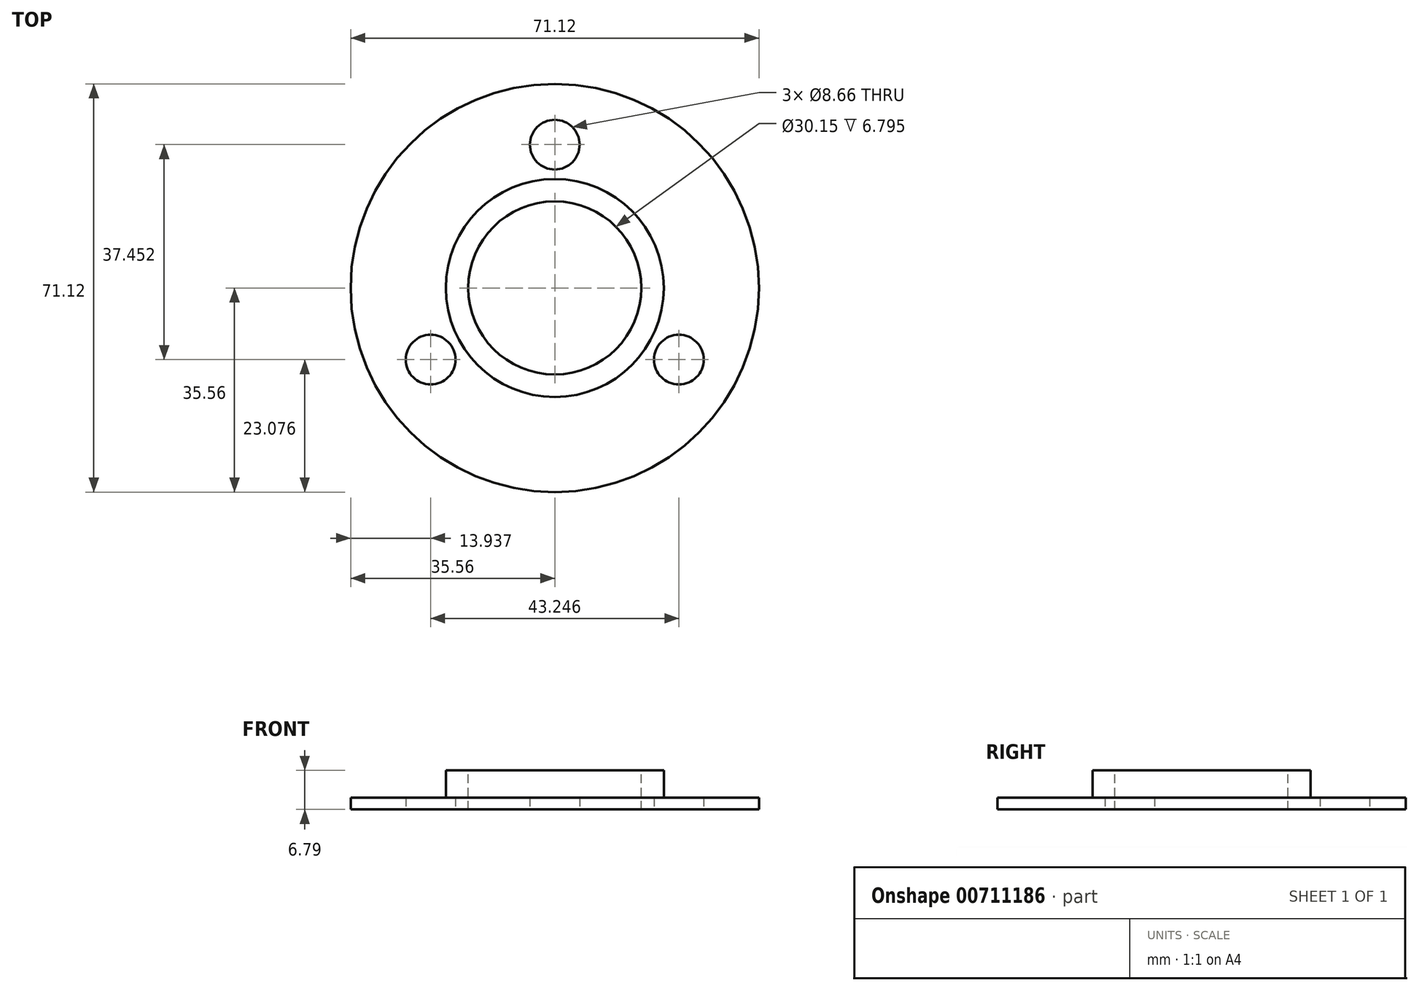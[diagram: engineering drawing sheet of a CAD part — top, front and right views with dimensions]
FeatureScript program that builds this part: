
annotation { "Feature Type Name" : "Feature", "Feature Type Description" : "" }
export const myFeature = defineFeature(function(context is Context, id is Id, definition is map)
    precondition{}
    {
        {
            var Q0;
            Q0=qCreatedBy(makeId("Top.planeOp"),FACE);
            var sketch = newSketch(context, id + "F0", { "sketchPlane" : qUnion([Q0])});
            skCircle(sketch, "E0", {"center": v(0, 0) * mm, "radius": 35.56 * mm});
            skCircle(sketch, "E1", {"center": v(0, 24.97) * mm, "radius": 4.33 * mm});
            skCircle(sketch, "E2.1.0", {"center": v(-21.62, -12.48) * mm, "radius": 4.33 * mm});
            skCircle(sketch, "E2.2.0", {"center": v(21.62, -12.48) * mm, "radius": 4.33 * mm});
            skSolve(sketch);
        }
        {
            var Q0;
            Q0=makeQuery(id+"F0.imprint","IMPRINT",FACE,{"disambiguationData":[TD([[makeQuery(id+"F0.imprint","IMPRINT",EDGE,{"derivedFrom":sQuery(id+"F0.wireOp",EDGE,"E0")}),1.0]])]});
            extrude(context, id + "F1", {"entities" : qUnion([Q0]), "depth" : 2.03 * mm, "offsetDistance" : 25.4 * mm});
        }
        {
            var Q0;
            Q0=makeQuery(id+"F1.opExtrude","CAP_FACE",FACE,{"disambiguationData":[OSD([sQuery(id+"F0.wireOp",EDGE,"E0"),sQuery(id+"F0.wireOp",EDGE,"E1"),sQuery(id+"F0.wireOp",EDGE,"E2.1.0"),sQuery(id+"F0.wireOp",EDGE,"E2.2.0")])],"isStart":false});
            var sketch = newSketch(context, id + "F2", { "sketchPlane" : qUnion([Q0])});
            skCircle(sketch, "E3", {"center": v(0, 0) * mm, "radius": 18.99 * mm});
            skSolve(sketch);
        }
        {
            var Q0;
            Q0 = qSketchRegion(id + "F2", true);
            extrude(context, id + "F3", {"entities" : qUnion([Q0]), "operationType" : NewBodyOperationType.ADD, "depth" : 4.76 * mm, "offsetDistance" : 25.4 * mm});
        }
        {
            var Q0;
            Q0=makeQuery(id+"F3.opExtrude","CAP_FACE",FACE,{"disambiguationData":[OSD([sQuery(id+"F2.wireOp",EDGE,"E3")])],"isStart":false});
            var sketch = newSketch(context, id + "F4", { "sketchPlane" : qUnion([Q0])});
            skCircle(sketch, "E4", {"center": v(0, 0) * mm, "radius": 15.07 * mm});
            skSolve(sketch);
        }
        {
            var Q0;
            Q0 = qSketchRegion(id + "F4", true);
            extrude(context, id + "F5", {"entities" : qUnion([Q0]), "operationType" : NewBodyOperationType.REMOVE, "endBound" : BoundingType.UP_TO_NEXT, "oppositeDirection" : true, "depth" : 25.4 * mm, "offsetDistance" : 25.4 * mm});
        }
    });
